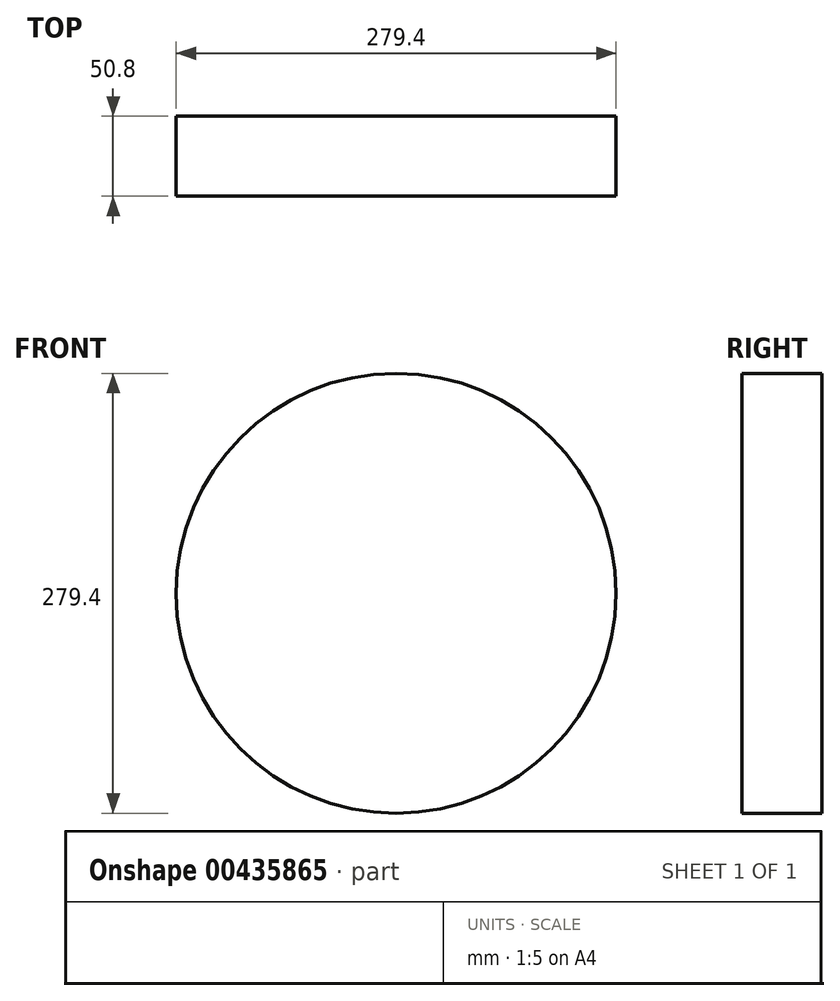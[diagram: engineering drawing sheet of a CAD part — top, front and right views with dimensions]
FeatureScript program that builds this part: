
annotation { "Feature Type Name" : "Feature", "Feature Type Description" : "" }
export const myFeature = defineFeature(function(context is Context, id is Id, definition is map)
    precondition{}
    {
        {
            var Q0;
            Q0=qCreatedBy(makeId("Front.planeOp"),FACE);
            var sketch = newSketch(context, id + "F0", { "sketchPlane" : qUnion([Q0])});
            skCircle(sketch, "E0", {"center": v(0, 0) * mm, "radius": 139.7 * mm});
            skSolve(sketch);
        }
        {
            var Q0;
            Q0=makeQuery(id+"F0.imprint","IMPRINT",FACE,{"disambiguationData":[TD([[makeQuery(id+"F0.imprint","IMPRINT",EDGE,{"derivedFrom":sQuery(id+"F0.wireOp",EDGE,"E0")}),1.0]])]});
            extrude(context, id + "F1", {"entities" : qUnion([Q0]), "depth" : 50.8 * mm});
        }
    });
